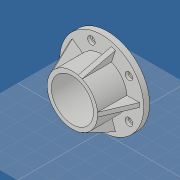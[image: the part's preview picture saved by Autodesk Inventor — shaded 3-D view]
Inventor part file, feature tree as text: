
AUTODESK INVENTOR PART (.ipt)
format: ipt  version: 2019 (Build 230136000, 136)  size: 186,880 bytes
history: native  units: mm
features: sketch x3, extrude x3, other x2, pattern_circular x2, hole x1
ambient origin geometry x8: Origin, YZ Plane, XZ Plane, XY Plane, X Axis, Y Axis, Z Axis, Center Point
bodies: Volumenkörper1 (feature_tree)
feature tree (11):
  other  "<userpath>\OneDrive\Dokumente\Inventor\Absauganlage\Absauganlage_Params.xlsx"
  sketch  "Skizze1"  dims[d0=50.2mm d1=100.0mm]
  extrude  "Extrusion1"  Depth=100.0mm
  extrude  "Extrusion2"  Depth=7.0mm TaperAngle=0.0deg
  extrude  "Extrusion3"  Depth=5.0mm
  pattern_circular  "Runde Anordnung1"  [2 undecoded]
  hole  "Bohrung1"  [1 undecoded]
  pattern_circular  "Runde Anordnung2"  Count=8  [1 undecoded]
  sketch  "Skizze2"  dims[d2=60.0mm d3=7.0mm d4=0.0mm]
  sketch  "Skizze3"  dims[d5=35.0mm d6=0.0mm d7=5.0mm d9=5.0mm d10=0.0mm d11=50.0mm d12=360.0deg d14=80.0mm d15=5.5mm d16=6.0mm d17=9.0mm d18=3.5mm d19=90.0deg d20=4.0mm d21=0.0mm d22=50.0mm d23=360.0deg]
  other  "Schnittkanten projizieren1"
note: 4 required parameter values undecoded (feature->parameter linkage not recoverable at this tier; creation-order binding heuristic only, values carry confidence <= 0.55)
